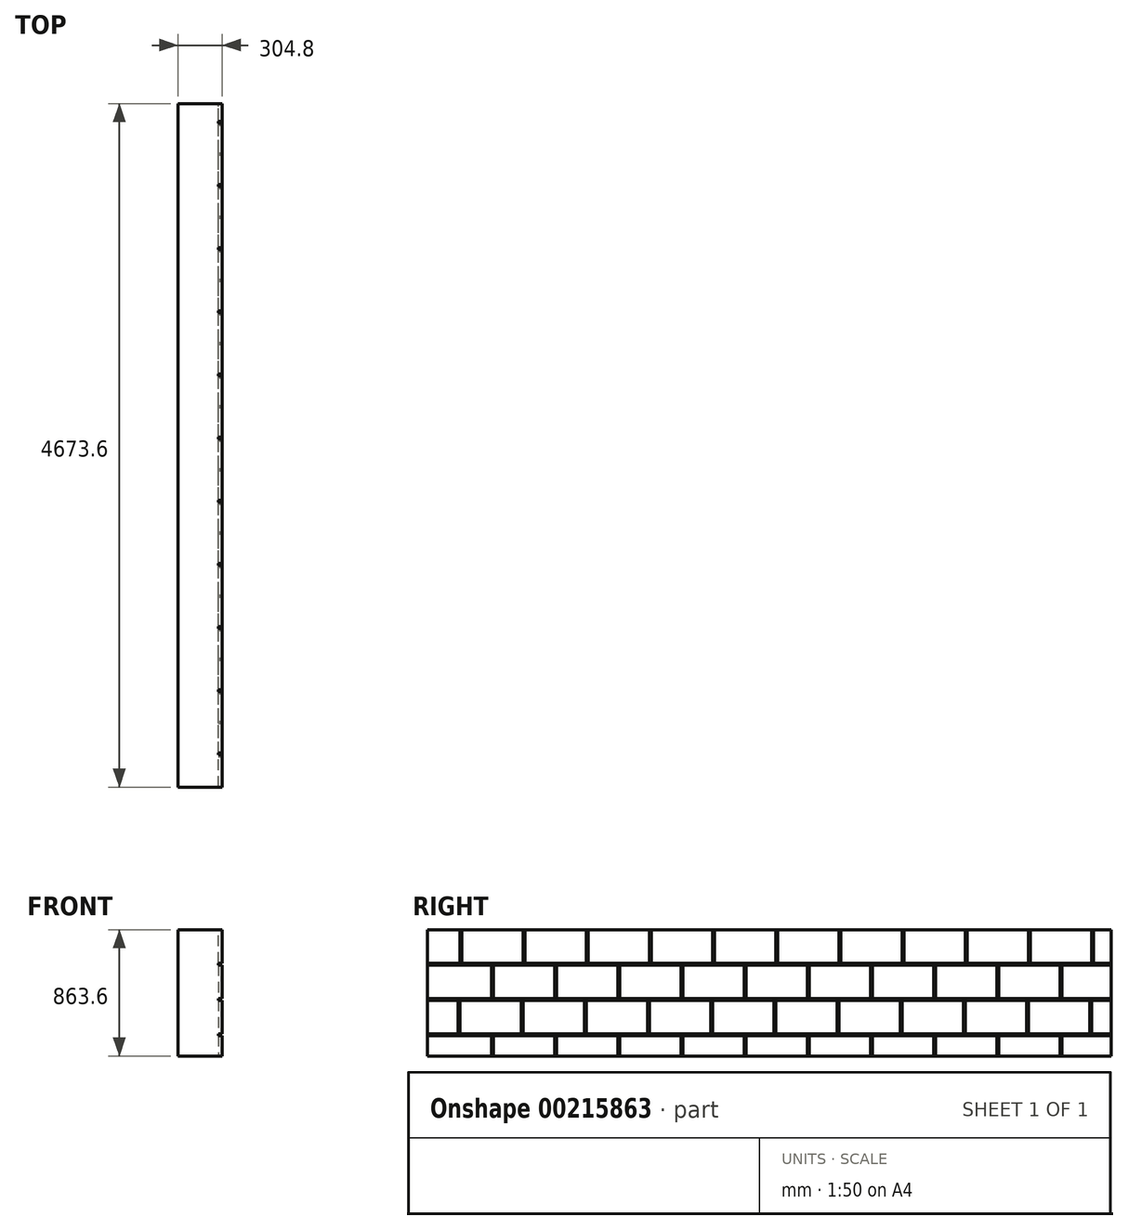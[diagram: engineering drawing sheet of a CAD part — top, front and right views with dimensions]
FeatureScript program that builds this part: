
annotation { "Feature Type Name" : "Feature", "Feature Type Description" : "" }
export const myFeature = defineFeature(function(context is Context, id is Id, definition is map)
    precondition{}
    {
        {
            var Q0;
            Q0=qCreatedBy(makeId("Right.planeOp"),FACE);
            var sketch = newSketch(context, id + "F0", { "sketchPlane" : qUnion([Q0])});
            skLineSegment(sketch, "E0.bottom", {"start": v(0, 0) * mm, "end": v(-4673.6, 0) * mm});
            skLineSegment(sketch, "E0.top", {"start": v(0, 863.6) * mm, "end": v(-4673.6, 863.6) * mm});
            skLineSegment(sketch, "E0.left", {"start": v(0, 0) * mm, "end": v(0, 863.6) * mm});
            skLineSegment(sketch, "E0.right", {"start": v(-4673.6, 0) * mm, "end": v(-4673.6, 863.6) * mm});
            skSolve(sketch);
        }
        {
            var Q0;
            Q0=makeQuery(id+"F0.imprint","IMPRINT",FACE,{"disambiguationData":[TD([[makeQuery(id+"F0.imprint","IMPRINT",EDGE,{"derivedFrom":sQuery(id+"F0.wireOp",EDGE,"E0.bottom")}),-1.0]])]});
            extrude(context, id + "F1", {"entities" : qUnion([Q0]), "depth" : 304.8 * mm});
        }
        {
            var Q0;
            Q0=makeQuery(id+"F1.opExtrude","CAP_FACE",FACE,{"disambiguationData":[OSD([sQuery(id+"F0.wireOp",EDGE,"E0.bottom"),sQuery(id+"F0.wireOp",EDGE,"E0.top"),sQuery(id+"F0.wireOp",EDGE,"E0.left"),sQuery(id+"F0.wireOp",EDGE,"E0.right")])],"isStart":false});
            var sketch = newSketch(context, id + "F2", { "sketchPlane" : qUnion([Q0])});
            skLineSegment(sketch, "E1.bottom", {"start": v(-4825.07, 635) * mm, "end": v(148.8, 635) * mm});
            skLineSegment(sketch, "E1.top", {"start": v(-4825.07, 622.3) * mm, "end": v(148.8, 622.3) * mm});
            skLineSegment(sketch, "E1.left", {"start": v(-4825.07, 635) * mm, "end": v(-4825.07, 622.3) * mm});
            skLineSegment(sketch, "E1.right", {"start": v(148.8, 635) * mm, "end": v(148.8, 622.3) * mm});
            skLineSegment(sketch, "E2.bottom", {"start": v(-4843.6, 393.7) * mm, "end": v(204.08, 393.7) * mm});
            skLineSegment(sketch, "E2.top", {"start": v(-4843.6, 381) * mm, "end": v(204.08, 381) * mm});
            skLineSegment(sketch, "E2.left", {"start": v(-4843.6, 393.7) * mm, "end": v(-4843.6, 381) * mm});
            skLineSegment(sketch, "E2.right", {"start": v(204.08, 393.7) * mm, "end": v(204.08, 381) * mm});
            skLineSegment(sketch, "E3.bottom", {"start": v(-4945.13, 152.4) * mm, "end": v(102.64, 152.4) * mm});
            skLineSegment(sketch, "E3.top", {"start": v(-4945.13, 139.7) * mm, "end": v(102.64, 139.7) * mm});
            skLineSegment(sketch, "E3.left", {"start": v(-4945.13, 152.4) * mm, "end": v(-4945.13, 139.7) * mm});
            skLineSegment(sketch, "E3.right", {"start": v(102.64, 152.4) * mm, "end": v(102.64, 139.7) * mm});
            skSolve(sketch);
        }
        {
            var Q0;
            Q0 = qSketchRegion(id + "F2", true);
            extrude(context, id + "F3", {"entities" : qUnion([Q0]), "operationType" : NewBodyOperationType.REMOVE, "oppositeDirection" : true, "depth" : 25.4 * mm});
        }
        {
            var Q0;
            {var subQ0=sQuery(id+"F0.wireOp",EDGE,"E0.top");var subQ1=sQuery(id+"F0.wireOp",EDGE,"E0.left");var subQ2=sQuery(id+"F0.wireOp",EDGE,"E0.right");Q0=makeQuery(id+"F3.boolean.opBoolean","SPLIT",FACE,{"disambiguationData":[TD([makeQuery(id+"F1.opExtrude","SWEPT_FACE",FACE,{"disambiguationData":[OSD([subQ0])]})])],"derivedFrom":makeQuery(id+"F1.opExtrude","CAP_FACE",FACE,{"disambiguationData":[OSD([sQuery(id+"F0.wireOp",EDGE,"E0.bottom"),subQ0,subQ1,subQ2])],"isStart":false})});}
            var sketch = newSketch(context, id + "F4", { "sketchPlane" : qUnion([Q0])});
            skLineSegment(sketch, "E4.bottom", {"start": v(-4439.89, 635) * mm, "end": v(-4452.59, 635) * mm});
            skLineSegment(sketch, "E4.top", {"start": v(-4439.89, 863.6) * mm, "end": v(-4452.59, 863.6) * mm});
            skLineSegment(sketch, "E4.left", {"start": v(-4439.89, 635) * mm, "end": v(-4439.89, 863.6) * mm});
            skLineSegment(sketch, "E4.right", {"start": v(-4452.59, 635) * mm, "end": v(-4452.59, 863.6) * mm});
            skLineSegment(sketch, "E5.bottom", {"start": v(-4236.69, 622.3) * mm, "end": v(-4223.99, 622.3) * mm});
            skLineSegment(sketch, "E5.top", {"start": v(-4236.69, 393.7) * mm, "end": v(-4223.99, 393.7) * mm});
            skLineSegment(sketch, "E5.left", {"start": v(-4236.69, 622.3) * mm, "end": v(-4236.69, 393.7) * mm});
            skLineSegment(sketch, "E5.right", {"start": v(-4223.99, 622.3) * mm, "end": v(-4223.99, 393.7) * mm});
            skLineSegment(sketch, "E6.bottom", {"start": v(-4465.29, 381) * mm, "end": v(-4452.59, 381) * mm});
            skLineSegment(sketch, "E6.top", {"start": v(-4465.29, 152.4) * mm, "end": v(-4452.59, 152.4) * mm});
            skLineSegment(sketch, "E6.left", {"start": v(-4465.29, 381) * mm, "end": v(-4465.29, 152.4) * mm});
            skLineSegment(sketch, "E6.right", {"start": v(-4452.59, 381) * mm, "end": v(-4452.59, 152.4) * mm});
            skLineSegment(sketch, "E7.bottom", {"start": v(-4236.69, 139.7) * mm, "end": v(-4223.99, 139.7) * mm});
            skLineSegment(sketch, "E7.top", {"start": v(-4236.69, 0) * mm, "end": v(-4223.99, 0) * mm});
            skLineSegment(sketch, "E7.left", {"start": v(-4236.69, 139.7) * mm, "end": v(-4236.69, 0) * mm});
            skLineSegment(sketch, "E7.right", {"start": v(-4223.99, 139.7) * mm, "end": v(-4223.99, 0) * mm});
            skLineSegment(sketch, "E8.1.0.0", {"start": v(-4033.49, 381) * mm, "end": v(-4033.49, 152.4) * mm});
            skLineSegment(sketch, "E8.1.0.1", {"start": v(-3792.19, 139.7) * mm, "end": v(-3792.19, 0) * mm});
            skLineSegment(sketch, "E8.1.0.2", {"start": v(-3792.19, 622.3) * mm, "end": v(-3792.19, 393.7) * mm});
            skLineSegment(sketch, "E8.1.0.3", {"start": v(-4020.79, 635) * mm, "end": v(-4020.79, 863.6) * mm});
            skLineSegment(sketch, "E8.1.0.4", {"start": v(-3804.89, 139.7) * mm, "end": v(-3804.89, 0) * mm});
            skLineSegment(sketch, "E8.1.0.5", {"start": v(-3804.89, 622.3) * mm, "end": v(-3804.89, 393.7) * mm});
            skLineSegment(sketch, "E8.1.0.6", {"start": v(-4008.09, 635) * mm, "end": v(-4008.09, 863.6) * mm});
            skLineSegment(sketch, "E8.1.0.7", {"start": v(-4020.79, 381) * mm, "end": v(-4020.79, 152.4) * mm});
            skLineSegment(sketch, "E8.1.0.8", {"start": v(-4033.49, 152.4) * mm, "end": v(-4020.79, 152.4) * mm});
            skLineSegment(sketch, "E8.1.0.9", {"start": v(-4033.49, 381) * mm, "end": v(-4020.79, 381) * mm});
            skLineSegment(sketch, "E8.1.0.10", {"start": v(-3804.89, 0) * mm, "end": v(-3792.19, 0) * mm});
            skLineSegment(sketch, "E8.1.0.11", {"start": v(-4008.09, 635) * mm, "end": v(-4020.79, 635) * mm});
            skLineSegment(sketch, "E8.1.0.12", {"start": v(-4008.09, 863.6) * mm, "end": v(-4020.79, 863.6) * mm});
            skLineSegment(sketch, "E8.1.0.13", {"start": v(-3804.89, 393.7) * mm, "end": v(-3792.19, 393.7) * mm});
            skLineSegment(sketch, "E8.1.0.14", {"start": v(-3804.89, 622.3) * mm, "end": v(-3792.19, 622.3) * mm});
            skLineSegment(sketch, "E8.1.0.15", {"start": v(-3804.89, 139.7) * mm, "end": v(-3792.19, 139.7) * mm});
            skLineSegment(sketch, "E8.2.0.0", {"start": v(-3601.69, 381) * mm, "end": v(-3601.69, 152.4) * mm});
            skLineSegment(sketch, "E8.2.0.1", {"start": v(-3360.39, 139.7) * mm, "end": v(-3360.39, 0) * mm});
            skLineSegment(sketch, "E8.2.0.2", {"start": v(-3360.39, 622.3) * mm, "end": v(-3360.39, 393.7) * mm});
            skLineSegment(sketch, "E8.2.0.3", {"start": v(-3588.99, 635) * mm, "end": v(-3588.99, 863.6) * mm});
            skLineSegment(sketch, "E8.2.0.4", {"start": v(-3373.09, 139.7) * mm, "end": v(-3373.09, 0) * mm});
            skLineSegment(sketch, "E8.2.0.5", {"start": v(-3373.09, 622.3) * mm, "end": v(-3373.09, 393.7) * mm});
            skLineSegment(sketch, "E8.2.0.6", {"start": v(-3576.29, 635) * mm, "end": v(-3576.29, 863.6) * mm});
            skLineSegment(sketch, "E8.2.0.7", {"start": v(-3588.99, 381) * mm, "end": v(-3588.99, 152.4) * mm});
            skLineSegment(sketch, "E8.2.0.8", {"start": v(-3601.69, 152.4) * mm, "end": v(-3588.99, 152.4) * mm});
            skLineSegment(sketch, "E8.2.0.9", {"start": v(-3601.69, 381) * mm, "end": v(-3588.99, 381) * mm});
            skLineSegment(sketch, "E8.2.0.10", {"start": v(-3373.09, 0) * mm, "end": v(-3360.39, 0) * mm});
            skLineSegment(sketch, "E8.2.0.11", {"start": v(-3576.29, 635) * mm, "end": v(-3588.99, 635) * mm});
            skLineSegment(sketch, "E8.2.0.12", {"start": v(-3576.29, 863.6) * mm, "end": v(-3588.99, 863.6) * mm});
            skLineSegment(sketch, "E8.2.0.13", {"start": v(-3373.09, 393.7) * mm, "end": v(-3360.39, 393.7) * mm});
            skLineSegment(sketch, "E8.2.0.14", {"start": v(-3373.09, 622.3) * mm, "end": v(-3360.39, 622.3) * mm});
            skLineSegment(sketch, "E8.2.0.15", {"start": v(-3373.09, 139.7) * mm, "end": v(-3360.39, 139.7) * mm});
            skLineSegment(sketch, "E8.3.0.0", {"start": v(-3169.89, 381) * mm, "end": v(-3169.89, 152.4) * mm});
            skLineSegment(sketch, "E8.3.0.1", {"start": v(-2928.59, 139.7) * mm, "end": v(-2928.59, 0) * mm});
            skLineSegment(sketch, "E8.3.0.2", {"start": v(-2928.59, 622.3) * mm, "end": v(-2928.59, 393.7) * mm});
            skLineSegment(sketch, "E8.3.0.3", {"start": v(-3157.19, 635) * mm, "end": v(-3157.19, 863.6) * mm});
            skLineSegment(sketch, "E8.3.0.4", {"start": v(-2941.29, 139.7) * mm, "end": v(-2941.29, 0) * mm});
            skLineSegment(sketch, "E8.3.0.5", {"start": v(-2941.29, 622.3) * mm, "end": v(-2941.29, 393.7) * mm});
            skLineSegment(sketch, "E8.3.0.6", {"start": v(-3144.49, 635) * mm, "end": v(-3144.49, 863.6) * mm});
            skLineSegment(sketch, "E8.3.0.7", {"start": v(-3157.19, 381) * mm, "end": v(-3157.19, 152.4) * mm});
            skLineSegment(sketch, "E8.3.0.8", {"start": v(-3169.89, 152.4) * mm, "end": v(-3157.19, 152.4) * mm});
            skLineSegment(sketch, "E8.3.0.9", {"start": v(-3169.89, 381) * mm, "end": v(-3157.19, 381) * mm});
            skLineSegment(sketch, "E8.3.0.10", {"start": v(-2941.29, 0) * mm, "end": v(-2928.59, 0) * mm});
            skLineSegment(sketch, "E8.3.0.11", {"start": v(-3144.49, 635) * mm, "end": v(-3157.19, 635) * mm});
            skLineSegment(sketch, "E8.3.0.12", {"start": v(-3144.49, 863.6) * mm, "end": v(-3157.19, 863.6) * mm});
            skLineSegment(sketch, "E8.3.0.13", {"start": v(-2941.29, 393.7) * mm, "end": v(-2928.59, 393.7) * mm});
            skLineSegment(sketch, "E8.3.0.14", {"start": v(-2941.29, 622.3) * mm, "end": v(-2928.59, 622.3) * mm});
            skLineSegment(sketch, "E8.3.0.15", {"start": v(-2941.29, 139.7) * mm, "end": v(-2928.59, 139.7) * mm});
            skLineSegment(sketch, "E8.4.0.0", {"start": v(-2738.09, 381) * mm, "end": v(-2738.09, 152.4) * mm});
            skLineSegment(sketch, "E8.4.0.1", {"start": v(-2496.79, 139.7) * mm, "end": v(-2496.79, 0) * mm});
            skLineSegment(sketch, "E8.4.0.2", {"start": v(-2496.79, 622.3) * mm, "end": v(-2496.79, 393.7) * mm});
            skLineSegment(sketch, "E8.4.0.3", {"start": v(-2725.39, 635) * mm, "end": v(-2725.39, 863.6) * mm});
            skLineSegment(sketch, "E8.4.0.4", {"start": v(-2509.49, 139.7) * mm, "end": v(-2509.49, 0) * mm});
            skLineSegment(sketch, "E8.4.0.5", {"start": v(-2509.49, 622.3) * mm, "end": v(-2509.49, 393.7) * mm});
            skLineSegment(sketch, "E8.4.0.6", {"start": v(-2712.69, 635) * mm, "end": v(-2712.69, 863.6) * mm});
            skLineSegment(sketch, "E8.4.0.7", {"start": v(-2725.39, 381) * mm, "end": v(-2725.39, 152.4) * mm});
            skLineSegment(sketch, "E8.4.0.8", {"start": v(-2738.09, 152.4) * mm, "end": v(-2725.39, 152.4) * mm});
            skLineSegment(sketch, "E8.4.0.9", {"start": v(-2738.09, 381) * mm, "end": v(-2725.39, 381) * mm});
            skLineSegment(sketch, "E8.4.0.10", {"start": v(-2509.49, 0) * mm, "end": v(-2496.79, 0) * mm});
            skLineSegment(sketch, "E8.4.0.11", {"start": v(-2712.69, 635) * mm, "end": v(-2725.39, 635) * mm});
            skLineSegment(sketch, "E8.4.0.12", {"start": v(-2712.69, 863.6) * mm, "end": v(-2725.39, 863.6) * mm});
            skLineSegment(sketch, "E8.4.0.13", {"start": v(-2509.49, 393.7) * mm, "end": v(-2496.79, 393.7) * mm});
            skLineSegment(sketch, "E8.4.0.14", {"start": v(-2509.49, 622.3) * mm, "end": v(-2496.79, 622.3) * mm});
            skLineSegment(sketch, "E8.4.0.15", {"start": v(-2509.49, 139.7) * mm, "end": v(-2496.79, 139.7) * mm});
            skLineSegment(sketch, "E8.5.0.0", {"start": v(-2306.29, 381) * mm, "end": v(-2306.29, 152.4) * mm});
            skLineSegment(sketch, "E8.5.0.1", {"start": v(-2064.99, 139.7) * mm, "end": v(-2064.99, 0) * mm});
            skLineSegment(sketch, "E8.5.0.2", {"start": v(-2064.99, 622.3) * mm, "end": v(-2064.99, 393.7) * mm});
            skLineSegment(sketch, "E8.5.0.3", {"start": v(-2293.59, 635) * mm, "end": v(-2293.59, 863.6) * mm});
            skLineSegment(sketch, "E8.5.0.4", {"start": v(-2077.69, 139.7) * mm, "end": v(-2077.69, 0) * mm});
            skLineSegment(sketch, "E8.5.0.5", {"start": v(-2077.69, 622.3) * mm, "end": v(-2077.69, 393.7) * mm});
            skLineSegment(sketch, "E8.5.0.6", {"start": v(-2280.89, 635) * mm, "end": v(-2280.89, 863.6) * mm});
            skLineSegment(sketch, "E8.5.0.7", {"start": v(-2293.59, 381) * mm, "end": v(-2293.59, 152.4) * mm});
            skLineSegment(sketch, "E8.5.0.8", {"start": v(-2306.29, 152.4) * mm, "end": v(-2293.59, 152.4) * mm});
            skLineSegment(sketch, "E8.5.0.9", {"start": v(-2306.29, 381) * mm, "end": v(-2293.59, 381) * mm});
            skLineSegment(sketch, "E8.5.0.10", {"start": v(-2077.69, 0) * mm, "end": v(-2064.99, 0) * mm});
            skLineSegment(sketch, "E8.5.0.11", {"start": v(-2280.89, 635) * mm, "end": v(-2293.59, 635) * mm});
            skLineSegment(sketch, "E8.5.0.12", {"start": v(-2280.89, 863.6) * mm, "end": v(-2293.59, 863.6) * mm});
            skLineSegment(sketch, "E8.5.0.13", {"start": v(-2077.69, 393.7) * mm, "end": v(-2064.99, 393.7) * mm});
            skLineSegment(sketch, "E8.5.0.14", {"start": v(-2077.69, 622.3) * mm, "end": v(-2064.99, 622.3) * mm});
            skLineSegment(sketch, "E8.5.0.15", {"start": v(-2077.69, 139.7) * mm, "end": v(-2064.99, 139.7) * mm});
            skLineSegment(sketch, "E8.6.0.0", {"start": v(-1874.49, 381) * mm, "end": v(-1874.49, 152.4) * mm});
            skLineSegment(sketch, "E8.6.0.1", {"start": v(-1633.19, 139.7) * mm, "end": v(-1633.19, 0) * mm});
            skLineSegment(sketch, "E8.6.0.2", {"start": v(-1633.19, 622.3) * mm, "end": v(-1633.19, 393.7) * mm});
            skLineSegment(sketch, "E8.6.0.3", {"start": v(-1861.79, 635) * mm, "end": v(-1861.79, 863.6) * mm});
            skLineSegment(sketch, "E8.6.0.4", {"start": v(-1645.89, 139.7) * mm, "end": v(-1645.89, 0) * mm});
            skLineSegment(sketch, "E8.6.0.5", {"start": v(-1645.89, 622.3) * mm, "end": v(-1645.89, 393.7) * mm});
            skLineSegment(sketch, "E8.6.0.6", {"start": v(-1849.09, 635) * mm, "end": v(-1849.09, 863.6) * mm});
            skLineSegment(sketch, "E8.6.0.7", {"start": v(-1861.79, 381) * mm, "end": v(-1861.79, 152.4) * mm});
            skLineSegment(sketch, "E8.6.0.8", {"start": v(-1874.49, 152.4) * mm, "end": v(-1861.79, 152.4) * mm});
            skLineSegment(sketch, "E8.6.0.9", {"start": v(-1874.49, 381) * mm, "end": v(-1861.79, 381) * mm});
            skLineSegment(sketch, "E8.6.0.10", {"start": v(-1645.89, 0) * mm, "end": v(-1633.19, 0) * mm});
            skLineSegment(sketch, "E8.6.0.11", {"start": v(-1849.09, 635) * mm, "end": v(-1861.79, 635) * mm});
            skLineSegment(sketch, "E8.6.0.12", {"start": v(-1849.09, 863.6) * mm, "end": v(-1861.79, 863.6) * mm});
            skLineSegment(sketch, "E8.6.0.13", {"start": v(-1645.89, 393.7) * mm, "end": v(-1633.19, 393.7) * mm});
            skLineSegment(sketch, "E8.6.0.14", {"start": v(-1645.89, 622.3) * mm, "end": v(-1633.19, 622.3) * mm});
            skLineSegment(sketch, "E8.6.0.15", {"start": v(-1645.89, 139.7) * mm, "end": v(-1633.19, 139.7) * mm});
            skLineSegment(sketch, "E8.7.0.0", {"start": v(-1442.69, 381) * mm, "end": v(-1442.69, 152.4) * mm});
            skLineSegment(sketch, "E8.7.0.1", {"start": v(-1201.39, 139.7) * mm, "end": v(-1201.39, 0) * mm});
            skLineSegment(sketch, "E8.7.0.2", {"start": v(-1201.39, 622.3) * mm, "end": v(-1201.39, 393.7) * mm});
            skLineSegment(sketch, "E8.7.0.3", {"start": v(-1429.99, 635) * mm, "end": v(-1429.99, 863.6) * mm});
            skLineSegment(sketch, "E8.7.0.4", {"start": v(-1214.09, 139.7) * mm, "end": v(-1214.09, 0) * mm});
            skLineSegment(sketch, "E8.7.0.5", {"start": v(-1214.09, 622.3) * mm, "end": v(-1214.09, 393.7) * mm});
            skLineSegment(sketch, "E8.7.0.6", {"start": v(-1417.29, 635) * mm, "end": v(-1417.29, 863.6) * mm});
            skLineSegment(sketch, "E8.7.0.7", {"start": v(-1429.99, 381) * mm, "end": v(-1429.99, 152.4) * mm});
            skLineSegment(sketch, "E8.7.0.8", {"start": v(-1442.69, 152.4) * mm, "end": v(-1429.99, 152.4) * mm});
            skLineSegment(sketch, "E8.7.0.9", {"start": v(-1442.69, 381) * mm, "end": v(-1429.99, 381) * mm});
            skLineSegment(sketch, "E8.7.0.10", {"start": v(-1214.09, 0) * mm, "end": v(-1201.39, 0) * mm});
            skLineSegment(sketch, "E8.7.0.11", {"start": v(-1417.29, 635) * mm, "end": v(-1429.99, 635) * mm});
            skLineSegment(sketch, "E8.7.0.12", {"start": v(-1417.29, 863.6) * mm, "end": v(-1429.99, 863.6) * mm});
            skLineSegment(sketch, "E8.7.0.13", {"start": v(-1214.09, 393.7) * mm, "end": v(-1201.39, 393.7) * mm});
            skLineSegment(sketch, "E8.7.0.14", {"start": v(-1214.09, 622.3) * mm, "end": v(-1201.39, 622.3) * mm});
            skLineSegment(sketch, "E8.7.0.15", {"start": v(-1214.09, 139.7) * mm, "end": v(-1201.39, 139.7) * mm});
            skLineSegment(sketch, "E8.8.0.0", {"start": v(-1010.89, 381) * mm, "end": v(-1010.89, 152.4) * mm});
            skLineSegment(sketch, "E8.8.0.1", {"start": v(-769.59, 139.7) * mm, "end": v(-769.59, 0) * mm});
            skLineSegment(sketch, "E8.8.0.2", {"start": v(-769.59, 622.3) * mm, "end": v(-769.59, 393.7) * mm});
            skLineSegment(sketch, "E8.8.0.3", {"start": v(-998.19, 635) * mm, "end": v(-998.19, 863.6) * mm});
            skLineSegment(sketch, "E8.8.0.4", {"start": v(-782.29, 139.7) * mm, "end": v(-782.29, 0) * mm});
            skLineSegment(sketch, "E8.8.0.5", {"start": v(-782.29, 622.3) * mm, "end": v(-782.29, 393.7) * mm});
            skLineSegment(sketch, "E8.8.0.6", {"start": v(-985.49, 635) * mm, "end": v(-985.49, 863.6) * mm});
            skLineSegment(sketch, "E8.8.0.7", {"start": v(-998.19, 381) * mm, "end": v(-998.19, 152.4) * mm});
            skLineSegment(sketch, "E8.8.0.8", {"start": v(-1010.89, 152.4) * mm, "end": v(-998.19, 152.4) * mm});
            skLineSegment(sketch, "E8.8.0.9", {"start": v(-1010.89, 381) * mm, "end": v(-998.19, 381) * mm});
            skLineSegment(sketch, "E8.8.0.10", {"start": v(-782.29, 0) * mm, "end": v(-769.59, 0) * mm});
            skLineSegment(sketch, "E8.8.0.11", {"start": v(-985.49, 635) * mm, "end": v(-998.19, 635) * mm});
            skLineSegment(sketch, "E8.8.0.12", {"start": v(-985.49, 863.6) * mm, "end": v(-998.19, 863.6) * mm});
            skLineSegment(sketch, "E8.8.0.13", {"start": v(-782.29, 393.7) * mm, "end": v(-769.59, 393.7) * mm});
            skLineSegment(sketch, "E8.8.0.14", {"start": v(-782.29, 622.3) * mm, "end": v(-769.59, 622.3) * mm});
            skLineSegment(sketch, "E8.8.0.15", {"start": v(-782.29, 139.7) * mm, "end": v(-769.59, 139.7) * mm});
            skLineSegment(sketch, "E8.9.0.0", {"start": v(-579.09, 381) * mm, "end": v(-579.09, 152.4) * mm});
            skLineSegment(sketch, "E8.9.0.1", {"start": v(-337.79, 139.7) * mm, "end": v(-337.79, 0) * mm});
            skLineSegment(sketch, "E8.9.0.2", {"start": v(-337.79, 622.3) * mm, "end": v(-337.79, 393.7) * mm});
            skLineSegment(sketch, "E8.9.0.3", {"start": v(-566.39, 635) * mm, "end": v(-566.39, 863.6) * mm});
            skLineSegment(sketch, "E8.9.0.4", {"start": v(-350.49, 139.7) * mm, "end": v(-350.49, 0) * mm});
            skLineSegment(sketch, "E8.9.0.5", {"start": v(-350.49, 622.3) * mm, "end": v(-350.49, 393.7) * mm});
            skLineSegment(sketch, "E8.9.0.6", {"start": v(-553.69, 635) * mm, "end": v(-553.69, 863.6) * mm});
            skLineSegment(sketch, "E8.9.0.7", {"start": v(-566.39, 381) * mm, "end": v(-566.39, 152.4) * mm});
            skLineSegment(sketch, "E8.9.0.8", {"start": v(-579.09, 152.4) * mm, "end": v(-566.39, 152.4) * mm});
            skLineSegment(sketch, "E8.9.0.9", {"start": v(-579.09, 381) * mm, "end": v(-566.39, 381) * mm});
            skLineSegment(sketch, "E8.9.0.10", {"start": v(-350.49, 0) * mm, "end": v(-337.79, 0) * mm});
            skLineSegment(sketch, "E8.9.0.11", {"start": v(-553.69, 635) * mm, "end": v(-566.39, 635) * mm});
            skLineSegment(sketch, "E8.9.0.12", {"start": v(-553.69, 863.6) * mm, "end": v(-566.39, 863.6) * mm});
            skLineSegment(sketch, "E8.9.0.13", {"start": v(-350.49, 393.7) * mm, "end": v(-337.79, 393.7) * mm});
            skLineSegment(sketch, "E8.9.0.14", {"start": v(-350.49, 622.3) * mm, "end": v(-337.79, 622.3) * mm});
            skLineSegment(sketch, "E8.9.0.15", {"start": v(-350.49, 139.7) * mm, "end": v(-337.79, 139.7) * mm});
            skLineSegment(sketch, "E8.10.0.0", {"start": v(-147.29, 381) * mm, "end": v(-147.29, 152.4) * mm});
            skLineSegment(sketch, "E8.10.0.1", {"start": v(94.01, 139.7) * mm, "end": v(94.01, 0) * mm});
            skLineSegment(sketch, "E8.10.0.2", {"start": v(94.01, 622.3) * mm, "end": v(94.01, 393.7) * mm});
            skLineSegment(sketch, "E8.10.0.3", {"start": v(-134.59, 635) * mm, "end": v(-134.59, 863.6) * mm});
            skLineSegment(sketch, "E8.10.0.4", {"start": v(81.31, 139.7) * mm, "end": v(81.31, 0) * mm});
            skLineSegment(sketch, "E8.10.0.5", {"start": v(81.31, 622.3) * mm, "end": v(81.31, 393.7) * mm});
            skLineSegment(sketch, "E8.10.0.6", {"start": v(-121.89, 635) * mm, "end": v(-121.89, 863.6) * mm});
            skLineSegment(sketch, "E8.10.0.7", {"start": v(-134.59, 381) * mm, "end": v(-134.59, 152.4) * mm});
            skLineSegment(sketch, "E8.10.0.8", {"start": v(-147.29, 152.4) * mm, "end": v(-134.59, 152.4) * mm});
            skLineSegment(sketch, "E8.10.0.9", {"start": v(-147.29, 381) * mm, "end": v(-134.59, 381) * mm});
            skLineSegment(sketch, "E8.10.0.10", {"start": v(81.31, 0) * mm, "end": v(94.01, 0) * mm});
            skLineSegment(sketch, "E8.10.0.11", {"start": v(-121.89, 635) * mm, "end": v(-134.59, 635) * mm});
            skLineSegment(sketch, "E8.10.0.12", {"start": v(-121.89, 863.6) * mm, "end": v(-134.59, 863.6) * mm});
            skLineSegment(sketch, "E8.10.0.13", {"start": v(81.31, 393.7) * mm, "end": v(94.01, 393.7) * mm});
            skLineSegment(sketch, "E8.10.0.14", {"start": v(81.31, 622.3) * mm, "end": v(94.01, 622.3) * mm});
            skLineSegment(sketch, "E8.10.0.15", {"start": v(81.31, 139.7) * mm, "end": v(94.01, 139.7) * mm});
            skLineSegment(sketch, "E8.direction1", {"start": v(-4465.29, 152.4) * mm, "end": v(-4033.49, 152.4) * mm, "construction": true});
            skSolve(sketch);
        }
        {
            var Q0;
            Q0 = qSketchRegion(id + "F4", true);
            extrude(context, id + "F5", {"entities" : qUnion([Q0]), "operationType" : NewBodyOperationType.REMOVE, "oppositeDirection" : true, "depth" : 25.4 * mm});
        }
    });
